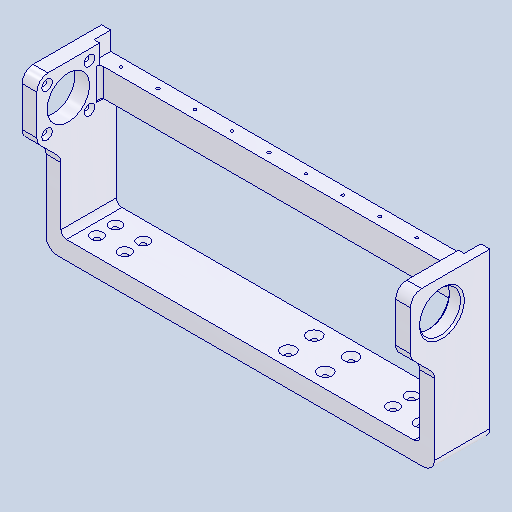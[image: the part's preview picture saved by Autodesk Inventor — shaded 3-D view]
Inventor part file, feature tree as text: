
AUTODESK INVENTOR PART (.ipt)
format: ipt  version: 2024 (Build 280153000, 153)  size: 227,328 bytes
history: native  units: mm
features: other x3, sketch x3
ambient origin geometry x8: Origin, YZ Plane, XZ Plane, XY Plane, X Axis, Y Axis, Z Axis, Center Point
bodies: Solid1 (feature_tree)
feature tree (6):
  other  "gantry_R.ipt"
  other  "Solid1::gantry_R.ipt"
  other  "TaggingFeature1"
  sketch  "Sketch1"  dims[d0=10.0mm]
  sketch  "Sketch2"
  sketch  "Sketch3"
